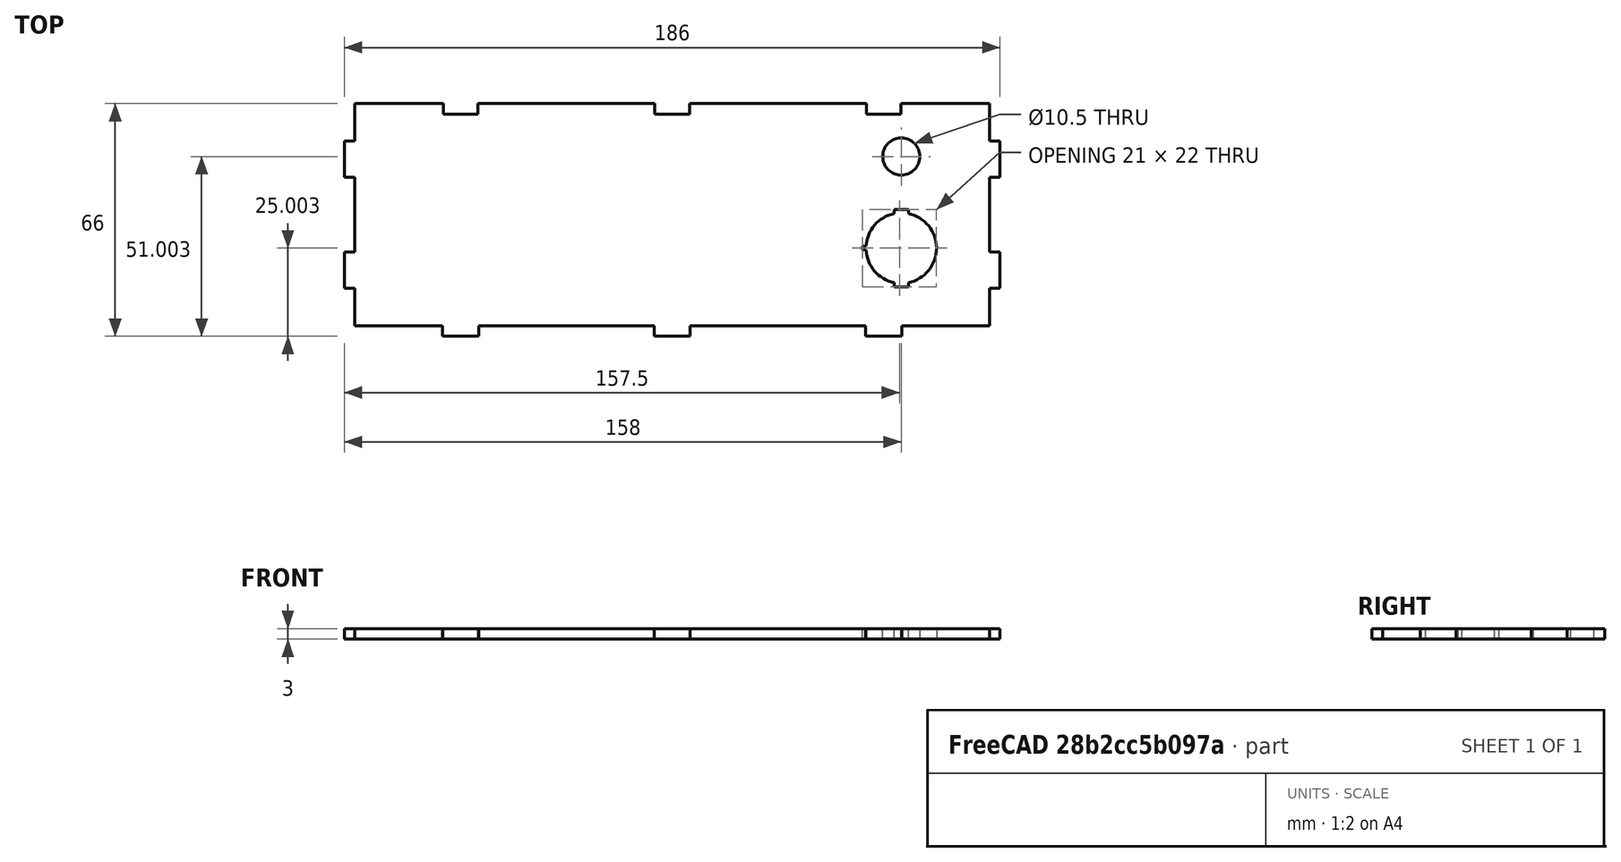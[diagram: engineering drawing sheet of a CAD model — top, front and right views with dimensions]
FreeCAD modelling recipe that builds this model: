
FCSTD DOCUMENT  (FreeCAD 1.0R38641 +468 (Git))
Label: point-controller-box-interface-v0.6.0
License: All rights reserved
LicenseURL: http://en.wikipedia.org/wiki/All_rights_reserved
objects: Part::Feature×7, Part::Part2DObjectPython×7, Sketcher::SketchObject×6, Part::Mirroring×1
note: 27 computed .brp shape members not serialized (recipe doc carries the construction recipe); baked Part::Feature solids carry a one-line shape summary decoded from their .brp

FEATURE [Part::Feature] test
  Placement = pos=(93,51,93) rot=(1,0,0;1.5708rad)
  shape: bbox 186 x 51 x 3 mm, 46 faces (baked)
FEATURE [Part::Feature] test001
  Placement = pos=(196,63,-60) rot=(0,1,0;1.5708rad)
  shape: bbox 63.37 x 126 x 3 mm, 38 faces (baked)
FEATURE [Part::Feature] test002
  Placement = pos=(93,206.207,88.2734) rot=(0.121054,0,0;3.02024rad)
  shape: bbox 186 x 126.9 x 3 mm, 56 faces (baked)
FEATURE [Part::Feature] test003
  Placement = pos=(196,199,123) rot=(0,1,0;1.5708rad)
  shape: bbox 63.37 x 126 x 3 mm, 38 faces (baked)
FEATURE [Part::Feature] test004
  Placement = pos=(93,338.933,-30) rot=(1,0,0;1.5708rad)
  shape: bbox 186 x 66 x 3 mm, 46 faces (baked)
FEATURE [Part::Feature] test005
  Placement = pos=(289,335.933,33) rot=(0,1,0;3.14159rad)
  shape: bbox 186 x 126 x 3 mm, 46 faces (baked)
FEATURE [Part::Feature] test006
  Placement = pos=(93,474.933,-30) rot=(1,0,0;1.5708rad)
  shape: bbox 186 x 66 x 3 mm, 59 faces (baked)
FEATURE [Part::Part2DObjectPython] Shape2DView  label="Shape2DView-Front"  # Draft 2D object (typed FeaturePython)
  AutoUpdate = true
  Base = -> test
  Clip = false
  FuseArch = false
  HiddenLines = false
  InPlace = true
  OnlySolids = false
  Projection = (0,0,1)
  ProjectionMode = 0
  SegmentLength = 0.05
  Tessellation = false
  VisibleOnly = false
FEATURE [Part::Part2DObjectPython] Shape2DView001  # Draft 2D object (typed FeaturePython)
  AutoUpdate = true
  Base = -> test001
  Clip = false
  FuseArch = false
  HiddenLines = false
  InPlace = true
  OnlySolids = false
  Projection = (0,0,1)
  ProjectionMode = 0
  SegmentLength = 0.05
  Tessellation = false
  VisibleOnly = false
FEATURE [Part::Part2DObjectPython] Shape2DView002  # Draft 2D object (typed FeaturePython)
  AutoUpdate = true
  Base = -> test002
  Clip = false
  FuseArch = false
  HiddenLines = false
  InPlace = true
  OnlySolids = false
  Projection = (0,0,1)
  ProjectionMode = 0
  SegmentLength = 0.05
  Tessellation = false
  VisibleOnly = false
FEATURE [Part::Part2DObjectPython] Shape2DView003  # Draft 2D object (typed FeaturePython)
  AutoUpdate = true
  Base = -> test003
  Clip = false
  FuseArch = false
  HiddenLines = false
  InPlace = true
  OnlySolids = false
  Projection = (0,0,1)
  ProjectionMode = 0
  SegmentLength = 0.05
  Tessellation = false
  VisibleOnly = false
FEATURE [Part::Part2DObjectPython] Shape2DView004  # Draft 2D object (typed FeaturePython)
  AutoUpdate = true
  Base = -> test004
  Clip = false
  FuseArch = false
  HiddenLines = false
  InPlace = true
  OnlySolids = false
  Projection = (0,0,1)
  ProjectionMode = 0
  SegmentLength = 0.05
  Tessellation = false
  VisibleOnly = false
FEATURE [Part::Part2DObjectPython] Shape2DView005  # Draft 2D object (typed FeaturePython)
  AutoUpdate = true
  Base = -> test005
  Clip = false
  FuseArch = false
  HiddenLines = false
  InPlace = true
  OnlySolids = false
  Projection = (0,0,1)
  ProjectionMode = 0
  SegmentLength = 0.05
  Tessellation = false
  VisibleOnly = false
FEATURE [Part::Part2DObjectPython] Shape2DView006  # Draft 2D object (typed FeaturePython)
  AutoUpdate = true
  Base = -> test006
  Clip = false
  FuseArch = false
  HiddenLines = false
  InPlace = true
  OnlySolids = false
  Projection = (0,0,1)
  ProjectionMode = 0
  SegmentLength = 0.05
  Tessellation = false
  VisibleOnly = false
FEATURE [Sketcher::SketchObject] Sketch  label="Sketch-Front"
  ArcFitTolerance = 0
  FullyConstrained = false
  MakeInternals = false
  sketch-geometry (44):
    g0: LineSegment StartX=3 StartY=51 StartZ=0 EndX=28.1 EndY=51 EndZ=0
    g1: LineSegment StartX=28.1 StartY=51 StartZ=0 EndX=28.1 EndY=47.95 EndZ=0
    g2: LineSegment StartX=3 StartY=44.1 StartZ=0 EndX=3 EndY=51 EndZ=0
    g3: LineSegment StartX=28.1 StartY=47.95 StartZ=0 EndX=37.9 EndY=47.95 EndZ=0
    g4: LineSegment StartX=37.9 StartY=51 StartZ=0 EndX=37.9 EndY=47.95 EndZ=0
    g5: LineSegment StartX=37.9 StartY=51 StartZ=0 EndX=88.1 EndY=51 EndZ=0
    g6: LineSegment StartX=88.1 StartY=51 StartZ=0 EndX=88.1 EndY=47.95 EndZ=0
    g7: LineSegment StartX=88.1 StartY=47.95 StartZ=0 EndX=97.9 EndY=47.95 EndZ=0
    g8: LineSegment StartX=97.9 StartY=51 StartZ=0 EndX=97.9 EndY=47.95 EndZ=0
    g9: LineSegment StartX=97.9 StartY=51 StartZ=0 EndX=148.1 EndY=51 EndZ=0
    g10: LineSegment StartX=148.1 StartY=51 StartZ=0 EndX=148.1 EndY=47.95 EndZ=0
    g11: LineSegment StartX=148.1 StartY=47.95 StartZ=0 EndX=157.9 EndY=47.95 EndZ=0
    g12: LineSegment StartX=157.9 StartY=51 StartZ=0 EndX=157.9 EndY=47.95 EndZ=0
    g13: LineSegment StartX=157.9 StartY=51 StartZ=0 EndX=183 EndY=51 EndZ=0
    g14: LineSegment StartX=183 StartY=51 StartZ=0 EndX=183 EndY=44.1 EndZ=0
    g15: LineSegment StartX=3 StartY=44.1 StartZ=0 EndX=0 EndY=44.1 EndZ=0
    g16: LineSegment StartX=183 StartY=44.1 StartZ=0 EndX=186 EndY=44.1 EndZ=0
    g17: LineSegment StartX=186 StartY=33.9 StartZ=0 EndX=186 EndY=44.1 EndZ=0
    g18: LineSegment StartX=183 StartY=33.9 StartZ=0 EndX=186 EndY=33.9 EndZ=0
    g19: LineSegment StartX=183 StartY=33.9 StartZ=0 EndX=183 EndY=20.1 EndZ=0
    g20: LineSegment StartX=183 StartY=20.1 StartZ=0 EndX=186 EndY=20.1 EndZ=0
    g21: LineSegment StartX=186 StartY=9.9 StartZ=0 EndX=186 EndY=20.1 EndZ=0
    g22: LineSegment StartX=183 StartY=9.9 StartZ=0 EndX=186 EndY=9.9 EndZ=0
    g23: LineSegment StartX=183 StartY=9.9 StartZ=0 EndX=183 EndY=3 EndZ=0
    g24: LineSegment StartX=183 StartY=3 StartZ=0 EndX=158.1 EndY=3 EndZ=0
    g25: LineSegment StartX=158.1 StartY=3 StartZ=0 EndX=158.1 EndY=1.69e-14 EndZ=0
    g26: LineSegment StartX=147.9 StartY=1.6e-14 StartZ=0 EndX=158.1 EndY=1.6e-14 EndZ=0
    g27: LineSegment StartX=147.9 StartY=3 StartZ=0 EndX=147.9 EndY=1.69e-14 EndZ=0
    g28: LineSegment StartX=147.9 StartY=3 StartZ=0 EndX=98.1 EndY=3 EndZ=0
    g29: LineSegment StartX=98.1 StartY=3 StartZ=0 EndX=98.1 EndY=7.1e-15 EndZ=0
    g30: LineSegment StartX=87.9 StartY=6.2e-15 StartZ=0 EndX=98.1 EndY=6.2e-15 EndZ=0
    g31: LineSegment StartX=87.9 StartY=3 StartZ=0 EndX=87.9 EndY=7.1e-15 EndZ=0
    g32: LineSegment StartX=87.9 StartY=3 StartZ=0 EndX=38.1 EndY=3 EndZ=0
    g33: LineSegment StartX=38.1 StartY=3 StartZ=0 EndX=38.1 EndY=-2.7e-15 EndZ=0
    g34: LineSegment StartX=27.9 StartY=-3.6e-15 StartZ=0 EndX=38.1 EndY=-3.6e-15 EndZ=0
    g35: LineSegment StartX=27.9 StartY=3 StartZ=0 EndX=27.9 EndY=-2.7e-15 EndZ=0
    g36: LineSegment StartX=27.9 StartY=3 StartZ=0 EndX=3 EndY=3 EndZ=0
    g37: LineSegment StartX=3 StartY=3 StartZ=0 EndX=3 EndY=9.9 EndZ=0
    g38: LineSegment StartX=3 StartY=9.9 StartZ=0 EndX=0 EndY=9.9 EndZ=0
    g39: LineSegment StartX=0 StartY=20.1 StartZ=0 EndX=0 EndY=9.9 EndZ=0
    g40: LineSegment StartX=3 StartY=20.1 StartZ=0 EndX=0 EndY=20.1 EndZ=0
    g41: LineSegment StartX=3 StartY=20.1 StartZ=0 EndX=3 EndY=33.9 EndZ=0
    g42: LineSegment StartX=3 StartY=33.9 StartZ=0 EndX=0 EndY=33.9 EndZ=0
    g43: LineSegment StartX=0 StartY=44.1 StartZ=0 EndX=0 EndY=33.9 EndZ=0
FEATURE [Part::Mirroring] Mirror  label="Shape2DView003 (mirrored)"
  Base = (309.469,126.906,35.2508)
  Normal = (0.997697,-0.0191098,0.0650815)
  Source = -> Shape2DView003
FEATURE [Sketcher::SketchObject] Sketch001  label="Sketch-Right"
  ArcFitTolerance = 0
  FullyConstrained = false
  MakeInternals = false
  Placement = pos=(5.21681,-0.0999223,-39.8313) rot=(-0.01915,-0.999817,0;0.130255rad)
  sketch-geometry (37):
    g0: LineSegment StartX=366.687 StartY=259.944 StartZ=0 EndX=377.895 EndY=259.515 EndZ=0
    g1: LineSegment StartX=377.778 StartY=256.467 StartZ=0 EndX=377.895 EndY=259.515 EndZ=0
    g2: LineSegment StartX=377.778 StartY=256.467 StartZ=0 EndX=387.571 EndY=256.092 EndZ=0
    g3: LineSegment StartX=387.571 StartY=256.092 StartZ=0 EndX=387.687 EndY=259.14 EndZ=0
    g4: LineSegment StartX=387.687 StartY=259.14 StartZ=0 EndX=409.371 EndY=258.309 EndZ=0
    g5: LineSegment StartX=409.255 StartY=255.261 StartZ=0 EndX=409.371 EndY=258.309 EndZ=0
    g6: LineSegment StartX=409.255 StartY=255.261 StartZ=0 EndX=419.047 EndY=254.886 EndZ=0
    g7: LineSegment StartX=419.047 StartY=254.886 StartZ=0 EndX=419.164 EndY=257.933 EndZ=0
    g8: LineSegment StartX=419.164 StartY=257.933 StartZ=0 EndX=430.006 EndY=257.518 EndZ=0
    g9: LineSegment StartX=430.006 StartY=257.518 StartZ=0 EndX=428.93 EndY=229.438 EndZ=0
    g10: LineSegment StartX=428.93 StartY=229.438 StartZ=0 EndX=425.882 EndY=229.555 EndZ=0
    g11: LineSegment StartX=425.507 StartY=219.762 StartZ=0 EndX=425.882 EndY=229.555 EndZ=0
    g12: LineSegment StartX=428.555 StartY=219.646 StartZ=0 EndX=425.507 EndY=219.762 EndZ=0
    g13: LineSegment StartX=428.555 StartY=219.646 StartZ=0 EndX=426.633 EndY=169.482 EndZ=0
    g14: LineSegment StartX=426.633 StartY=169.482 StartZ=0 EndX=423.585 EndY=169.599 EndZ=0
    g15: LineSegment StartX=423.21 StartY=159.806 StartZ=0 EndX=423.585 EndY=169.599 EndZ=0
    g16: LineSegment StartX=426.257 StartY=159.69 StartZ=0 EndX=423.21 EndY=159.806 EndZ=0
    g17: LineSegment StartX=425.181 StartY=131.61 StartZ=0 EndX=418.087 EndY=131.882 EndZ=0
    g18: LineSegment StartX=418.087 StartY=131.882 StartZ=0 EndX=418.203 EndY=134.93 EndZ=0
    g19: LineSegment StartX=426.257 StartY=159.69 StartZ=0 EndX=425.181 EndY=131.61 EndZ=0
    g20: LineSegment StartX=408.41 StartY=135.305 StartZ=0 EndX=418.203 EndY=134.93 EndZ=0
    g21: LineSegment StartX=408.294 StartY=132.257 StartZ=0 EndX=408.41 EndY=135.305 EndZ=0
    g22: LineSegment StartX=408.294 StartY=132.257 StartZ=0 EndX=394.104 EndY=132.801 EndZ=0
    g23: LineSegment StartX=394.104 StartY=132.801 StartZ=0 EndX=394.221 EndY=135.849 EndZ=0
    g24: LineSegment StartX=384.428 StartY=136.224 StartZ=0 EndX=394.221 EndY=135.849 EndZ=0
    g25: LineSegment StartX=384.311 StartY=133.176 StartZ=0 EndX=384.428 EndY=136.224 EndZ=0
    g26: LineSegment StartX=384.311 StartY=133.176 StartZ=0 EndX=377.216 EndY=133.448 EndZ=0
    g27: LineSegment StartX=377.216 StartY=133.448 StartZ=0 EndX=375.07 EndY=159.237 EndZ=0
    g28: LineSegment StartX=375.07 StartY=159.237 StartZ=0 EndX=372.08 EndY=158.988 EndZ=0
    g29: LineSegment StartX=371.234 StartY=169.153 StartZ=0 EndX=372.08 EndY=158.988 EndZ=0
    g30: LineSegment StartX=374.224 StartY=169.402 StartZ=0 EndX=371.234 EndY=169.153 EndZ=0
    g31: LineSegment StartX=374.224 StartY=169.402 StartZ=0 EndX=369.93 EndY=220.979 EndZ=0
    g32: LineSegment StartX=369.93 StartY=220.979 StartZ=0 EndX=366.941 EndY=220.73 EndZ=0
    g33: LineSegment StartX=366.095 StartY=230.895 StartZ=0 EndX=366.941 EndY=220.73 EndZ=0
    g34: LineSegment StartX=369.084 StartY=231.144 StartZ=0 EndX=366.095 EndY=230.895 EndZ=0
    g35: LineSegment StartX=369.084 StartY=231.144 StartZ=0 EndX=366.938 EndY=256.933 EndZ=0
    g36: LineSegment StartX=366.938 StartY=256.933 StartZ=0 EndX=366.687 EndY=259.944 EndZ=0
FEATURE [Sketcher::SketchObject] Sketch002  label="Sketch-Left"
  ArcFitTolerance = 0
  FullyConstrained = false
  MakeInternals = false
  sketch-geometry (37):
    g0: LineSegment StartX=259.366 StartY=126 StartZ=0 EndX=248.15 EndY=126 EndZ=0
    g1: LineSegment StartX=248.15 StartY=122.95 StartZ=0 EndX=248.15 EndY=126 EndZ=0
    g2: LineSegment StartX=238.35 StartY=122.95 StartZ=0 EndX=248.15 EndY=122.95 EndZ=0
    g3: LineSegment StartX=238.35 StartY=122.95 StartZ=0 EndX=238.35 EndY=126 EndZ=0
    g4: LineSegment StartX=238.35 StartY=126 StartZ=0 EndX=216.65 EndY=126 EndZ=0
    g5: LineSegment StartX=216.65 StartY=122.95 StartZ=0 EndX=216.65 EndY=126 EndZ=0
    g6: LineSegment StartX=206.85 StartY=122.95 StartZ=0 EndX=216.65 EndY=122.95 EndZ=0
    g7: LineSegment StartX=206.85 StartY=122.95 StartZ=0 EndX=206.85 EndY=126 EndZ=0
    g8: LineSegment StartX=206.85 StartY=126 StartZ=0 EndX=196 EndY=126 EndZ=0
    g9: LineSegment StartX=196 StartY=126 StartZ=0 EndX=196 EndY=97.9 EndZ=0
    g10: LineSegment StartX=196 StartY=97.9 StartZ=0 EndX=199.05 EndY=97.9 EndZ=0
    g11: LineSegment StartX=199.05 StartY=97.9 StartZ=0 EndX=199.05 EndY=88.1 EndZ=0
    g12: LineSegment StartX=196 StartY=88.1 StartZ=0 EndX=199.05 EndY=88.1 EndZ=0
    g13: LineSegment StartX=196 StartY=88.1 StartZ=0 EndX=196 EndY=37.9 EndZ=0
    g14: LineSegment StartX=196 StartY=37.9 StartZ=0 EndX=199.05 EndY=37.9 EndZ=0
    g15: LineSegment StartX=199.05 StartY=37.9 StartZ=0 EndX=199.05 EndY=28.1 EndZ=0
    g16: LineSegment StartX=196 StartY=28.1 StartZ=0 EndX=199.05 EndY=28.1 EndZ=0
    g17: LineSegment StartX=196 StartY=7.1e-15 StartZ=0 EndX=203.1 EndY=6.1e-15 EndZ=0
    g18: LineSegment StartX=203.1 StartY=9.5e-15 StartZ=0 EndX=203.1 EndY=3.05 EndZ=0
    g19: LineSegment StartX=196 StartY=28.1 StartZ=0 EndX=196 EndY=0 EndZ=0
    g20: LineSegment StartX=203.1 StartY=3.05 StartZ=0 EndX=212.9 EndY=3.05 EndZ=0
    g21: LineSegment StartX=212.9 StartY=7.3e-15 StartZ=0 EndX=212.9 EndY=3.05 EndZ=0
    g22: LineSegment StartX=212.9 StartY=4.6e-15 StartZ=0 EndX=227.1 EndY=2.5e-15 EndZ=0
    g23: LineSegment StartX=227.1 StartY=-2.9e-15 StartZ=0 EndX=227.1 EndY=3.05 EndZ=0
    g24: LineSegment StartX=227.1 StartY=3.05 StartZ=0 EndX=236.9 EndY=3.05 EndZ=0
    g25: LineSegment StartX=236.9 StartY=-5.1e-15 StartZ=0 EndX=236.9 EndY=3.05 EndZ=0
    g26: LineSegment StartX=236.9 StartY=1.1e-15 StartZ=0 EndX=244 EndY=0 EndZ=0
    g27: LineSegment StartX=244 StartY=0 StartZ=0 EndX=247.133 EndY=25.6875 EndZ=0
    g28: LineSegment StartX=247.133 StartY=25.6875 StartZ=0 EndX=250.111 EndY=25.3243 EndZ=0
    g29: LineSegment StartX=251.345 StartY=35.4493 StartZ=0 EndX=250.111 EndY=25.3243 EndZ=0
    g30: LineSegment StartX=248.367 StartY=35.8125 StartZ=0 EndX=251.345 EndY=35.4493 EndZ=0
    g31: LineSegment StartX=248.367 StartY=35.8125 StartZ=0 EndX=254.633 EndY=87.1875 EndZ=0
    g32: LineSegment StartX=254.633 StartY=87.1875 StartZ=0 EndX=257.611 EndY=86.8243 EndZ=0
    g33: LineSegment StartX=258.845 StartY=96.9493 StartZ=0 EndX=257.611 EndY=86.8243 EndZ=0
    g34: LineSegment StartX=255.867 StartY=97.3125 StartZ=0 EndX=258.845 EndY=96.9493 EndZ=0
    g35: LineSegment StartX=255.867 StartY=97.3125 StartZ=0 EndX=259 EndY=123 EndZ=0
    g36: LineSegment StartX=259 StartY=123 StartZ=0 EndX=259.366 EndY=126 EndZ=0
FEATURE [Sketcher::SketchObject] Sketch003  label="Sketch-Top"
  ArcFitTolerance = 0
  FullyConstrained = false
  MakeInternals = false
  sketch-geometry (60):
    g0: LineSegment StartX=0 StartY=262.933 StartZ=0 EndX=28.1 EndY=262.933 EndZ=0
    g1: LineSegment StartX=37.9 StartY=262.933 StartZ=0 EndX=88.1 EndY=262.933 EndZ=0
    g2: LineSegment StartX=97.9 StartY=262.933 StartZ=0 EndX=148.1 EndY=262.933 EndZ=0
    g3: LineSegment StartX=157.9 StartY=262.933 StartZ=0 EndX=186 EndY=262.93 EndZ=0
    g4: LineSegment StartX=0 StartY=236.856 StartZ=0 EndX=0 EndY=262.933 EndZ=0
    g5: LineSegment StartX=5.1e-15 StartY=236.856 StartZ=0 EndX=3.05 EndY=236.856 EndZ=0
    g6: LineSegment StartX=3.05 StartY=227.056 StartZ=0 EndX=3.05 EndY=236.856 EndZ=0
    g7: LineSegment StartX=5.1e-15 StartY=227.056 StartZ=0 EndX=3.05 EndY=227.056 EndZ=0
    g8: LineSegment StartX=0 StartY=174.9 StartZ=0 EndX=0 EndY=227.056 EndZ=0
    g9: LineSegment StartX=5.6e-15 StartY=174.9 StartZ=0 EndX=3.05 EndY=174.9 EndZ=0
    g10: LineSegment StartX=3.05 StartY=165.1 StartZ=0 EndX=3.05 EndY=174.9 EndZ=0
    g11: LineSegment StartX=5.6e-15 StartY=165.1 StartZ=0 EndX=3.05 EndY=165.1 EndZ=0
    g12: LineSegment StartX=0 StartY=136 StartZ=0 EndX=0 EndY=165.1 EndZ=0
    g13: LineSegment StartX=28.1 StartY=136 StartZ=0 EndX=0 EndY=136 EndZ=0
    g14: LineSegment StartX=28.1 StartY=139.022 StartZ=0 EndX=28.1 EndY=136 EndZ=0
    g15: LineSegment StartX=37.9 StartY=139.022 StartZ=0 EndX=28.1 EndY=139.022 EndZ=0
    g16: LineSegment StartX=37.9 StartY=139.022 StartZ=0 EndX=37.9 EndY=136 EndZ=0
    g17: LineSegment StartX=88.1 StartY=136 StartZ=0 EndX=37.9 EndY=136 EndZ=0
    g18: LineSegment StartX=88.1 StartY=139.022 StartZ=0 EndX=88.1 EndY=136 EndZ=0
    g19: LineSegment StartX=97.9 StartY=139.022 StartZ=0 EndX=88.1 EndY=139.022 EndZ=0
    g20: LineSegment StartX=97.9 StartY=139.022 StartZ=0 EndX=97.9 EndY=136 EndZ=0
    g21: LineSegment StartX=148.1 StartY=136 StartZ=0 EndX=97.9 EndY=136 EndZ=0
    g22: LineSegment StartX=148.1 StartY=139.022 StartZ=0 EndX=148.1 EndY=136 EndZ=0
    g23: LineSegment StartX=157.9 StartY=139.022 StartZ=0 EndX=148.1 EndY=139.022 EndZ=0
    g24: LineSegment StartX=157.9 StartY=139.022 StartZ=0 EndX=157.9 EndY=136 EndZ=0
    g25: LineSegment StartX=186 StartY=136 StartZ=0 EndX=157.9 EndY=136 EndZ=0
    g26: LineSegment StartX=186 StartY=165.1 StartZ=0 EndX=186 EndY=136 EndZ=0
    g27: LineSegment StartX=183.241 StartY=165.1 StartZ=0 EndX=186 EndY=165.1 EndZ=0
    g28: ArcOfCircle CenterX=183.057 CenterY=165.207 CenterZ=0 NormalX=0 NormalY=0 NormalZ=1 AngleXU=0 Radius=0.213333 StartAngle=2.0944 EndAngle=5.75959
    g29: LineSegment StartX=182.95 StartY=165.391 StartZ=0 EndX=182.95 EndY=174.609 EndZ=0
    g30: ArcOfCircle CenterX=183.057 CenterY=174.793 CenterZ=0 NormalX=0 NormalY=0 NormalZ=1 AngleXU=0 Radius=0.213333 StartAngle=0.523599 EndAngle=4.18879
    g31: LineSegment StartX=183.241 StartY=174.9 StartZ=0 EndX=186 EndY=174.9 EndZ=0
    g32: LineSegment StartX=186 StartY=227.056 StartZ=0 EndX=186 EndY=174.9 EndZ=0
    g33: LineSegment StartX=183.241 StartY=227.056 StartZ=0 EndX=186 EndY=227.056 EndZ=0
    g34: ArcOfCircle CenterX=183.057 CenterY=227.162 CenterZ=0 NormalX=0 NormalY=0 NormalZ=1 AngleXU=0 Radius=0.213333 StartAngle=2.0944 EndAngle=5.75959
    g35: LineSegment StartX=182.95 StartY=227.347 StartZ=0 EndX=182.95 EndY=236.564 EndZ=0
    g36: ArcOfCircle CenterX=183.057 CenterY=236.749 CenterZ=0 NormalX=0 NormalY=0 NormalZ=1 AngleXU=0 Radius=0.213333 StartAngle=0.523599 EndAngle=4.18879
    g37: LineSegment StartX=183.241 StartY=236.856 StartZ=0 EndX=186 EndY=236.856 EndZ=0
    g38: LineSegment StartX=186 StartY=262.933 StartZ=0 EndX=186 EndY=236.856 EndZ=0
    g39: LineSegment StartX=157.9 StartY=262.933 StartZ=0 EndX=157.9 EndY=259.861 EndZ=0
    g40: LineSegment StartX=157.9 StartY=259.861 StartZ=0 EndX=148.1 EndY=259.861 EndZ=0
    g41: LineSegment StartX=148.1 StartY=262.933 StartZ=0 EndX=148.1 EndY=259.861 EndZ=0
    g42: LineSegment StartX=97.9 StartY=262.933 StartZ=0 EndX=97.9 EndY=259.861 EndZ=0
    g43: LineSegment StartX=97.9 StartY=259.861 StartZ=0 EndX=88.1 EndY=259.861 EndZ=0
    g44: LineSegment StartX=88.1 StartY=262.933 StartZ=0 EndX=88.1 EndY=259.861 EndZ=0
    g45: LineSegment StartX=37.9 StartY=262.933 StartZ=0 EndX=37.9 EndY=259.861 EndZ=0
    g46: LineSegment StartX=37.9 StartY=259.861 StartZ=0 EndX=28.1 EndY=259.861 EndZ=0
    g47: LineSegment StartX=28.1 StartY=262.933 StartZ=0 EndX=28.1 EndY=259.861 EndZ=0
    g48: LineSegment StartX=28.1 StartY=262.62 StartZ=0 EndX=28.1 EndY=259.861 EndZ=0
    g49: LineSegment StartX=37.9 StartY=262.62 StartZ=0 EndX=37.9 EndY=259.861 EndZ=0
    g50: LineSegment StartX=88.1 StartY=262.62 StartZ=0 EndX=88.1 EndY=259.861 EndZ=0
    g51: LineSegment StartX=97.9 StartY=262.62 StartZ=0 EndX=97.9 EndY=259.861 EndZ=0
    g52: LineSegment StartX=148.1 StartY=262.62 StartZ=0 EndX=148.1 EndY=259.861 EndZ=0
    g53: LineSegment StartX=157.9 StartY=262.62 StartZ=0 EndX=157.9 EndY=259.861 EndZ=0
    g54: LineSegment StartX=28.1 StartY=139.022 StartZ=0 EndX=28.1 EndY=138.709 EndZ=0
    g55: LineSegment StartX=37.9 StartY=139.022 StartZ=0 EndX=37.9 EndY=138.709 EndZ=0
    g56: LineSegment StartX=88.1 StartY=139.022 StartZ=0 EndX=88.1 EndY=138.709 EndZ=0
    g57: LineSegment StartX=97.9 StartY=139.022 StartZ=0 EndX=97.9 EndY=138.709 EndZ=0
    g58: LineSegment StartX=148.1 StartY=139.022 StartZ=0 EndX=148.1 EndY=138.709 EndZ=0
    g59: LineSegment StartX=157.9 StartY=139.022 StartZ=0 EndX=157.9 EndY=138.709 EndZ=0
  constraints (4):
    c: DistanceY(g12) = 136
    c: DistanceX(g12) = 0
    c: DistanceY(g3) = 262.93
    c: DistanceX(g3) = 186
FEATURE [Sketcher::SketchObject] Sketch004  label="Sketch-Base"
  ArcFitTolerance = 0
  FullyConstrained = false
  MakeInternals = false
  sketch-geometry (48):
    g0: LineSegment StartX=379 StartY=395.933 StartZ=0 EndX=354.1 EndY=395.933 EndZ=0
    g1: LineSegment StartX=354.1 StartY=395.933 StartZ=0 EndX=354.1 EndY=398.933 EndZ=0
    g2: LineSegment StartX=379 StartY=371.033 StartZ=0 EndX=379 EndY=395.933 EndZ=0
    g3: LineSegment StartX=343.9 StartY=398.933 StartZ=0 EndX=354.1 EndY=398.933 EndZ=0
    g4: LineSegment StartX=379 StartY=371.033 StartZ=0 EndX=382 EndY=371.033 EndZ=0
    g5: LineSegment StartX=343.9 StartY=395.933 StartZ=0 EndX=343.9 EndY=398.933 EndZ=0
    g6: LineSegment StartX=343.9 StartY=395.933 StartZ=0 EndX=294.1 EndY=395.933 EndZ=0
    g7: LineSegment StartX=294.1 StartY=395.933 StartZ=0 EndX=294.1 EndY=398.933 EndZ=0
    g8: LineSegment StartX=283.9 StartY=398.933 StartZ=0 EndX=294.1 EndY=398.933 EndZ=0
    g9: LineSegment StartX=283.9 StartY=395.933 StartZ=0 EndX=283.9 EndY=398.933 EndZ=0
    g10: LineSegment StartX=283.9 StartY=395.933 StartZ=0 EndX=234.1 EndY=395.933 EndZ=0
    g11: LineSegment StartX=234.1 StartY=395.933 StartZ=0 EndX=234.1 EndY=398.933 EndZ=0
    g12: LineSegment StartX=223.9 StartY=398.933 StartZ=0 EndX=234.1 EndY=398.933 EndZ=0
    g13: LineSegment StartX=223.9 StartY=395.933 StartZ=0 EndX=223.9 EndY=398.933 EndZ=0
    g14: LineSegment StartX=223.9 StartY=395.933 StartZ=0 EndX=199 EndY=395.93 EndZ=0
    g15: LineSegment StartX=199 StartY=395.93 StartZ=0 EndX=199 EndY=371.033 EndZ=0
    g16: LineSegment StartX=199 StartY=371.033 StartZ=0 EndX=196 EndY=371.033 EndZ=0
    g17: LineSegment StartX=196 StartY=360.833 StartZ=0 EndX=196 EndY=371.033 EndZ=0
    g18: LineSegment StartX=199 StartY=360.833 StartZ=0 EndX=196 EndY=360.833 EndZ=0
    g19: LineSegment StartX=199 StartY=360.833 StartZ=0 EndX=199 EndY=311.033 EndZ=0
    g20: LineSegment StartX=199 StartY=311.033 StartZ=0 EndX=196 EndY=311.033 EndZ=0
    g21: LineSegment StartX=196 StartY=300.833 StartZ=0 EndX=196 EndY=311.033 EndZ=0
    g22: LineSegment StartX=199 StartY=300.833 StartZ=0 EndX=196 EndY=300.833 EndZ=0
    g23: LineSegment StartX=199 StartY=300.833 StartZ=0 EndX=199 EndY=275.933 EndZ=0
    g24: LineSegment StartX=199 StartY=275.933 StartZ=0 EndX=223.9 EndY=275.933 EndZ=0
    g25: LineSegment StartX=223.9 StartY=275.933 StartZ=0 EndX=223.9 EndY=272.933 EndZ=0
    g26: LineSegment StartX=234.1 StartY=272.933 StartZ=0 EndX=223.9 EndY=272.933 EndZ=0
    g27: LineSegment StartX=234.1 StartY=275.933 StartZ=0 EndX=234.1 EndY=272.933 EndZ=0
    g28: LineSegment StartX=234.1 StartY=275.933 StartZ=0 EndX=283.9 EndY=275.933 EndZ=0
    g29: LineSegment StartX=283.9 StartY=275.933 StartZ=0 EndX=283.9 EndY=272.933 EndZ=0
    g30: LineSegment StartX=294.1 StartY=272.933 StartZ=0 EndX=283.9 EndY=272.933 EndZ=0
    g31: LineSegment StartX=294.1 StartY=275.933 StartZ=0 EndX=294.1 EndY=272.933 EndZ=0
    g32: LineSegment StartX=294.1 StartY=275.933 StartZ=0 EndX=343.9 EndY=275.933 EndZ=0
    g33: LineSegment StartX=343.9 StartY=275.933 StartZ=0 EndX=343.9 EndY=272.933 EndZ=0
    g34: LineSegment StartX=354.1 StartY=272.933 StartZ=0 EndX=343.9 EndY=272.933 EndZ=0
    g35: LineSegment StartX=354.1 StartY=275.933 StartZ=0 EndX=354.1 EndY=272.933 EndZ=0
    g36: LineSegment StartX=354.1 StartY=275.933 StartZ=0 EndX=379 EndY=275.93 EndZ=0
    g37: LineSegment StartX=379 StartY=275.93 StartZ=0 EndX=379 EndY=300.833 EndZ=0
    g38: LineSegment StartX=379 StartY=300.833 StartZ=0 EndX=382 EndY=300.833 EndZ=0
    g39: LineSegment StartX=382 StartY=311.033 StartZ=0 EndX=382 EndY=300.833 EndZ=0
    g40: LineSegment StartX=379 StartY=311.033 StartZ=0 EndX=382 EndY=311.033 EndZ=0
    g41: LineSegment StartX=379 StartY=311.033 StartZ=0 EndX=379 EndY=360.833 EndZ=0
    g42: LineSegment StartX=379 StartY=360.833 StartZ=0 EndX=382 EndY=360.833 EndZ=0
    g43: LineSegment StartX=382 StartY=371.033 StartZ=0 EndX=382 EndY=360.833 EndZ=0
    g44: Circle CenterX=274 CenterY=360.93 CenterZ=0 NormalX=0 NormalY=0 NormalZ=1 AngleXU=0 Radius=1.6
    g45: Circle CenterX=307 CenterY=360.93 CenterZ=0 NormalX=0 NormalY=0 NormalZ=1 AngleXU=0 Radius=1.6
    g46: Circle CenterX=274 CenterY=300.93 CenterZ=0 NormalX=0 NormalY=0 NormalZ=1 AngleXU=0 Radius=1.6
    g47: Circle CenterX=307 CenterY=300.93 CenterZ=0 NormalX=0 NormalY=0 NormalZ=1 AngleXU=0 Radius=1.6
  constraints (18):
    c: Coincident(g37,g36)
    c: DistanceX(g36) = 379
    c: DistanceY(g36) = 275.93
    c: Coincident(g15,g14)
    c: DistanceX(g14) = 199
    c: DistanceY(g14) = 395.93
    c: DistanceX(g14,g44) = 75
    c: DistanceY(g44,g14) = 35
    c: Horizontal(g44,g45)
    c: Horizontal(g46,g47)
    c: Vertical(g45,g47)
    c: Vertical(g44,g46)
    c: DistanceX(g44,g45) = 33
    c: DistanceY(g46,g44) = 60
    c: Equal(g46,g47)
    c: Equal(g46,g45)
    c: Equal(g46,g44)
    c: Diameter(g46) = 3.2
FEATURE [Sketcher::SketchObject] Sketch005  label="Sketch-Rear"
  ArcFitTolerance = 0
  FullyConstrained = false
  MakeInternals = false
  sketch-geometry (50):
    g0: LineSegment StartX=3 StartY=474.93 StartZ=0 EndX=28.1 EndY=474.933 EndZ=0
    g1: LineSegment StartX=28.1 StartY=474.933 StartZ=0 EndX=28.1 EndY=471.88 EndZ=0
    g2: LineSegment StartX=3 StartY=464.283 StartZ=0 EndX=3 EndY=474.93 EndZ=0
    g3: LineSegment StartX=37.9 StartY=471.883 StartZ=0 EndX=28.1 EndY=471.883 EndZ=0
    g4: LineSegment StartX=37.9 StartY=474.933 StartZ=0 EndX=37.9 EndY=471.883 EndZ=0
    g5: LineSegment StartX=37.9 StartY=474.933 StartZ=0 EndX=88.1 EndY=474.933 EndZ=0
    g6: LineSegment StartX=88.1 StartY=474.933 StartZ=0 EndX=88.1 EndY=471.883 EndZ=0
    g7: LineSegment StartX=97.9 StartY=471.883 StartZ=0 EndX=88.1 EndY=471.883 EndZ=0
    g8: LineSegment StartX=97.9 StartY=474.933 StartZ=0 EndX=97.9 EndY=471.883 EndZ=0
    g9: LineSegment StartX=97.9 StartY=474.933 StartZ=0 EndX=148.1 EndY=474.933 EndZ=0
    g10: LineSegment StartX=148.1 StartY=474.933 StartZ=0 EndX=148.1 EndY=471.883 EndZ=0
    g11: LineSegment StartX=157.9 StartY=471.883 StartZ=0 EndX=148.1 EndY=471.883 EndZ=0
    g12: LineSegment StartX=157.9 StartY=474.933 StartZ=0 EndX=157.9 EndY=471.883 EndZ=0
    g13: LineSegment StartX=157.9 StartY=474.933 StartZ=0 EndX=183 EndY=474.933 EndZ=0
    g14: LineSegment StartX=183 StartY=474.933 StartZ=0 EndX=183 EndY=464.283 EndZ=0
    g15: LineSegment StartX=3 StartY=464.283 StartZ=0 EndX=0 EndY=464.283 EndZ=0
    g16: LineSegment StartX=0 StartY=464.283 StartZ=0 EndX=0 EndY=454.083 EndZ=0
    g17: LineSegment StartX=3 StartY=432.783 StartZ=0 EndX=3 EndY=454.083 EndZ=0
    g18: LineSegment StartX=3 StartY=454.083 StartZ=0 EndX=0 EndY=454.083 EndZ=0
    g19: LineSegment StartX=3 StartY=432.783 StartZ=0 EndX=0 EndY=432.783 EndZ=0
    g20: LineSegment StartX=0 StartY=432.783 StartZ=0 EndX=0 EndY=422.583 EndZ=0
    g21: LineSegment StartX=3 StartY=411.933 StartZ=0 EndX=3 EndY=422.583 EndZ=0
    g22: LineSegment StartX=27.9 StartY=411.933 StartZ=0 EndX=3 EndY=411.933 EndZ=0
    g23: LineSegment StartX=3 StartY=422.583 StartZ=0 EndX=0 EndY=422.583 EndZ=0
    g24: LineSegment StartX=27.9 StartY=411.933 StartZ=0 EndX=27.9 EndY=408.933 EndZ=0
    g25: LineSegment StartX=27.9 StartY=408.933 StartZ=0 EndX=38.1 EndY=408.933 EndZ=0
    g26: LineSegment StartX=87.9 StartY=411.933 StartZ=0 EndX=38.1 EndY=411.933 EndZ=0
    g27: LineSegment StartX=38.1 StartY=411.933 StartZ=0 EndX=38.1 EndY=408.933 EndZ=0
    g28: LineSegment StartX=87.9 StartY=411.933 StartZ=0 EndX=87.9 EndY=408.933 EndZ=0
    g29: LineSegment StartX=87.9 StartY=408.933 StartZ=0 EndX=98.1 EndY=408.933 EndZ=0
    g30: LineSegment StartX=147.9 StartY=411.933 StartZ=0 EndX=98.1 EndY=411.933 EndZ=0
    g31: LineSegment StartX=98.1 StartY=411.933 StartZ=0 EndX=98.1 EndY=408.933 EndZ=0
    g32: LineSegment StartX=147.9 StartY=411.933 StartZ=0 EndX=147.9 EndY=408.933 EndZ=0
    g33: LineSegment StartX=147.9 StartY=408.933 StartZ=0 EndX=158.1 EndY=408.933 EndZ=0
    g34: LineSegment StartX=183 StartY=411.933 StartZ=0 EndX=158.1 EndY=411.933 EndZ=0
    g35: LineSegment StartX=183 StartY=422.583 StartZ=0 EndX=183 EndY=411.933 EndZ=0
    g36: LineSegment StartX=158.1 StartY=411.933 StartZ=0 EndX=158.1 EndY=408.933 EndZ=0
    g37: LineSegment StartX=183 StartY=422.583 StartZ=0 EndX=186 EndY=422.583 EndZ=0
    g38: LineSegment StartX=183 StartY=464.283 StartZ=0 EndX=186 EndY=464.283 EndZ=0
    g39: LineSegment StartX=186 StartY=422.583 StartZ=0 EndX=186 EndY=432.783 EndZ=0
    g40: LineSegment StartX=183 StartY=454.083 StartZ=0 EndX=183 EndY=432.783 EndZ=0
    g41: LineSegment StartX=183 StartY=432.783 StartZ=0 EndX=186 EndY=432.783 EndZ=0
    g42: LineSegment StartX=186 StartY=454.083 StartZ=0 EndX=186 EndY=464.283 EndZ=0
    g43: LineSegment StartX=183 StartY=454.083 StartZ=0 EndX=186 EndY=454.083 EndZ=0
    g44: GeomPoint [constr] X=4 Y=467.88 Z=0
    g45: GeomPoint [constr] X=4 Y=453.38 Z=0
    g46: LineSegment StartX=84 StartY=439.414 StartZ=0 EndX=101.2 EndY=439.414 EndZ=0
    g47: LineSegment StartX=101.2 StartY=439.414 StartZ=0 EndX=101.2 EndY=457.214 EndZ=0
    g48: LineSegment StartX=101.2 StartY=457.214 StartZ=0 EndX=84 EndY=457.214 EndZ=0
    g49: LineSegment StartX=84 StartY=457.214 StartZ=0 EndX=84 EndY=439.414 EndZ=0
  constraints (20):
    c: Coincident(g2,g0)
    c: DistanceY(g0) = 474.93
    c: DistanceX(g0) = 3
    c: DistanceX(g0,g44) = 1
    c: Vertical(g45,g44)
    c: DistanceY(g1) = 471.88
    c: DistanceX(g1) = 28.1
    c: DistanceY(g44,g1) = 4
    c: DistanceY(g45,g1) = 18.5
    c: Coincident(g46,g47)
    c: Coincident(g47,g48)
    c: Coincident(g48,g49)
    c: Coincident(g49,g46)
    c: Horizontal(g46)
    c: Horizontal(g48)
    c: Vertical(g47)
    c: Vertical(g49)
    c: DistanceX(g44,g48) = 80
    c: DistanceX(g48,g48) = 17.2
    c: DistanceY(g47,g47) = 17.8
